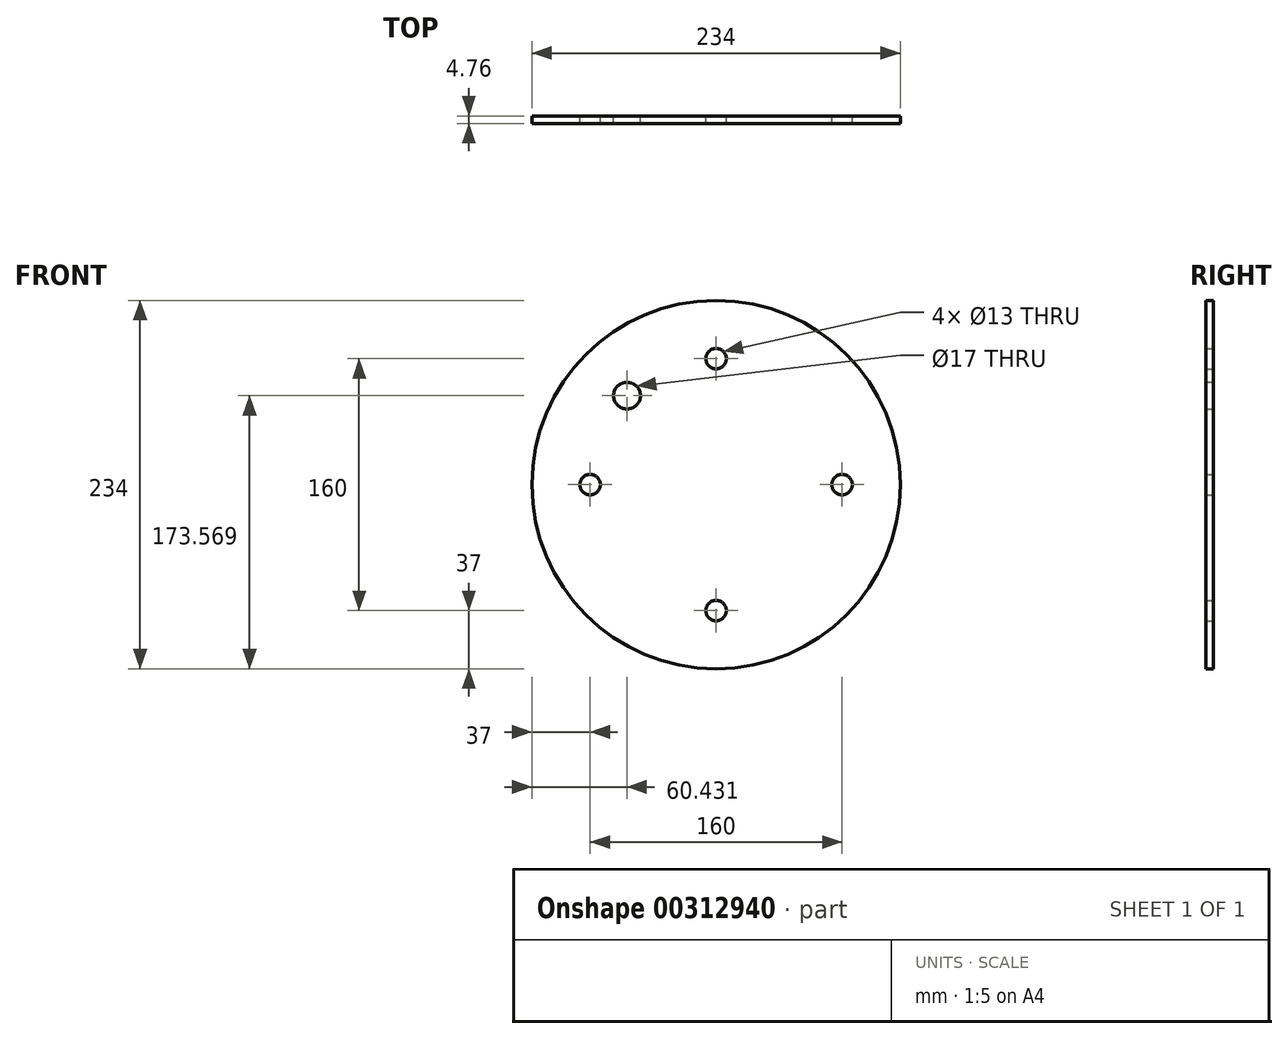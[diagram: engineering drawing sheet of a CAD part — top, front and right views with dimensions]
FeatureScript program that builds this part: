
annotation { "Feature Type Name" : "Feature", "Feature Type Description" : "" }
export const myFeature = defineFeature(function(context is Context, id is Id, definition is map)
    precondition{}
    {
        {
            var Q0;
            Q0=qCreatedBy(makeId("Front.planeOp"),FACE);
            var sketch = newSketch(context, id + "F0", { "sketchPlane" : qUnion([Q0])});
            skCircle(sketch, "E0", {"center": v(0, 0) * mm, "radius": 117 * mm});
            skPoint(sketch, "E1", {"position": v(0, 80) * mm});
            skPoint(sketch, "E2", {"position": v(80, 0) * mm});
            skPoint(sketch, "E3", {"position": v(0, -80) * mm});
            skPoint(sketch, "E4", {"position": v(-80, 0) * mm});
            skCircle(sketch, "E5", {"center": v(0, 80) * mm, "radius": 6.5 * mm});
            skCircle(sketch, "E6", {"center": v(80, 0) * mm, "radius": 6.5 * mm});
            skCircle(sketch, "E7", {"center": v(0, -80) * mm, "radius": 6.5 * mm});
            skCircle(sketch, "E8", {"center": v(-80, 0) * mm, "radius": 6.5 * mm});
            skPoint(sketch, "E9", {"position": v(-56.57, 56.57) * mm});
            skCircle(sketch, "E10", {"center": v(-56.57, 56.57) * mm, "radius": 8.5 * mm});
            skSolve(sketch);
        }
        {
            var Q0;
            Q0 = qSketchRegion(id + "F0", true);
            extrude(context, id + "F1", {"entities" : qUnion([Q0]), "depth" : 4.76 * mm});
        }
    });
